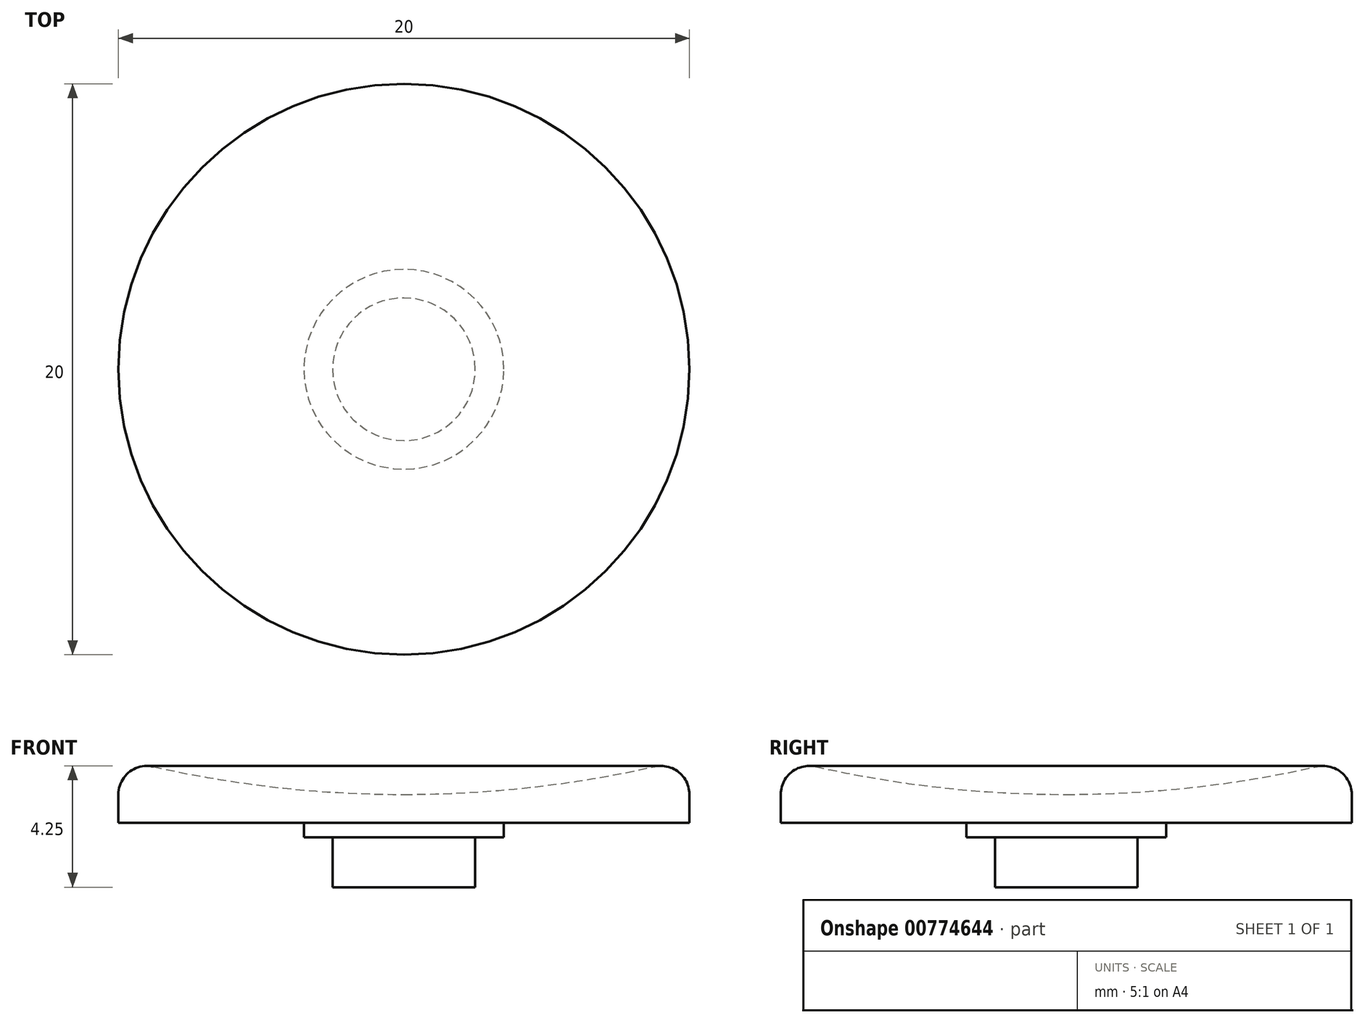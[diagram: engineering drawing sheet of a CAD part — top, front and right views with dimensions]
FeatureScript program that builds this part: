
annotation { "Feature Type Name" : "Feature", "Feature Type Description" : "" }
export const myFeature = defineFeature(function(context is Context, id is Id, definition is map)
    precondition{}
    {
        {
            var Q0;
            Q0=qCreatedBy(makeId("Front.planeOp"),FACE);
            var sketch = newSketch(context, id + "F0", { "sketchPlane" : qUnion([Q0])});
            skLineSegment(sketch, "E0", {"start": v(-2.5, 0.25) * mm, "end": v(-2.5, 2) * mm});
            skLineSegment(sketch, "E1", {"start": v(-2.5, 2) * mm, "end": v(-3.5, 2) * mm});
            skLineSegment(sketch, "E2", {"start": v(-3.5, 2) * mm, "end": v(-3.5, 2.5) * mm});
            skLineSegment(sketch, "E3", {"start": v(-3.5, 2.5) * mm, "end": v(-10, 2.5) * mm});
            skLineSegment(sketch, "E4", {"start": v(-10, 2.5) * mm, "end": v(-10, 3.5) * mm});
            skLineSegment(sketch, "E5", {"start": v(0, 0.25) * mm, "end": v(0, 3.5) * mm});
            skArc(sketch, "E6", {"start": v(-8.78, 4.48) * mm, "mid": v(-9.62, 4.28) * mm, "end": v(-10, 3.5) * mm});
            skArc(sketch, "E7", {"start": v(-8.78, 4.48) * mm, "mid": v(-4.42, 3.74) * mm, "end": v(0, 3.5) * mm});
            skLineSegment(sketch, "E8", {"start": v(-2.5, 0.25) * mm, "end": v(0, 0.25) * mm});
            skPoint(sketch, "E9.orphan", {"position": v(0, 0) * mm});
            skSolve(sketch);
        }
        {
            var Q0;
            Q0=qCreatedBy(makeId("Front.planeOp"),FACE);
            var sketch = newSketch(context, id + "F1", { "sketchPlane" : qUnion([Q0])});
            skLineSegment(sketch, "E10", {"start": v(0, -21.55) * mm, "end": v(0, 31.93) * mm});
            skSolve(sketch);
        }
        {
            var Q0;
            Q0=makeQuery(id+"F0.imprint","IMPRINT",FACE,{"disambiguationData":[TD([[makeQuery(id+"F0.imprint","IMPRINT",EDGE,{"derivedFrom":sQuery(id+"F0.wireOp",EDGE,"E0")}),-1.0]])]});
            var Q1;
            Q1=sQuery(id+"F1.wireOp",EDGE,"E10");
            revolve(context, id + "F2", {"surfaceOperationType" : NewSurfaceOperationType.NEW, "entities" : qUnion([Q0]), "axis" : qUnion([Q1]), "revolveType" : RevolveType.FULL});
        }
    });
